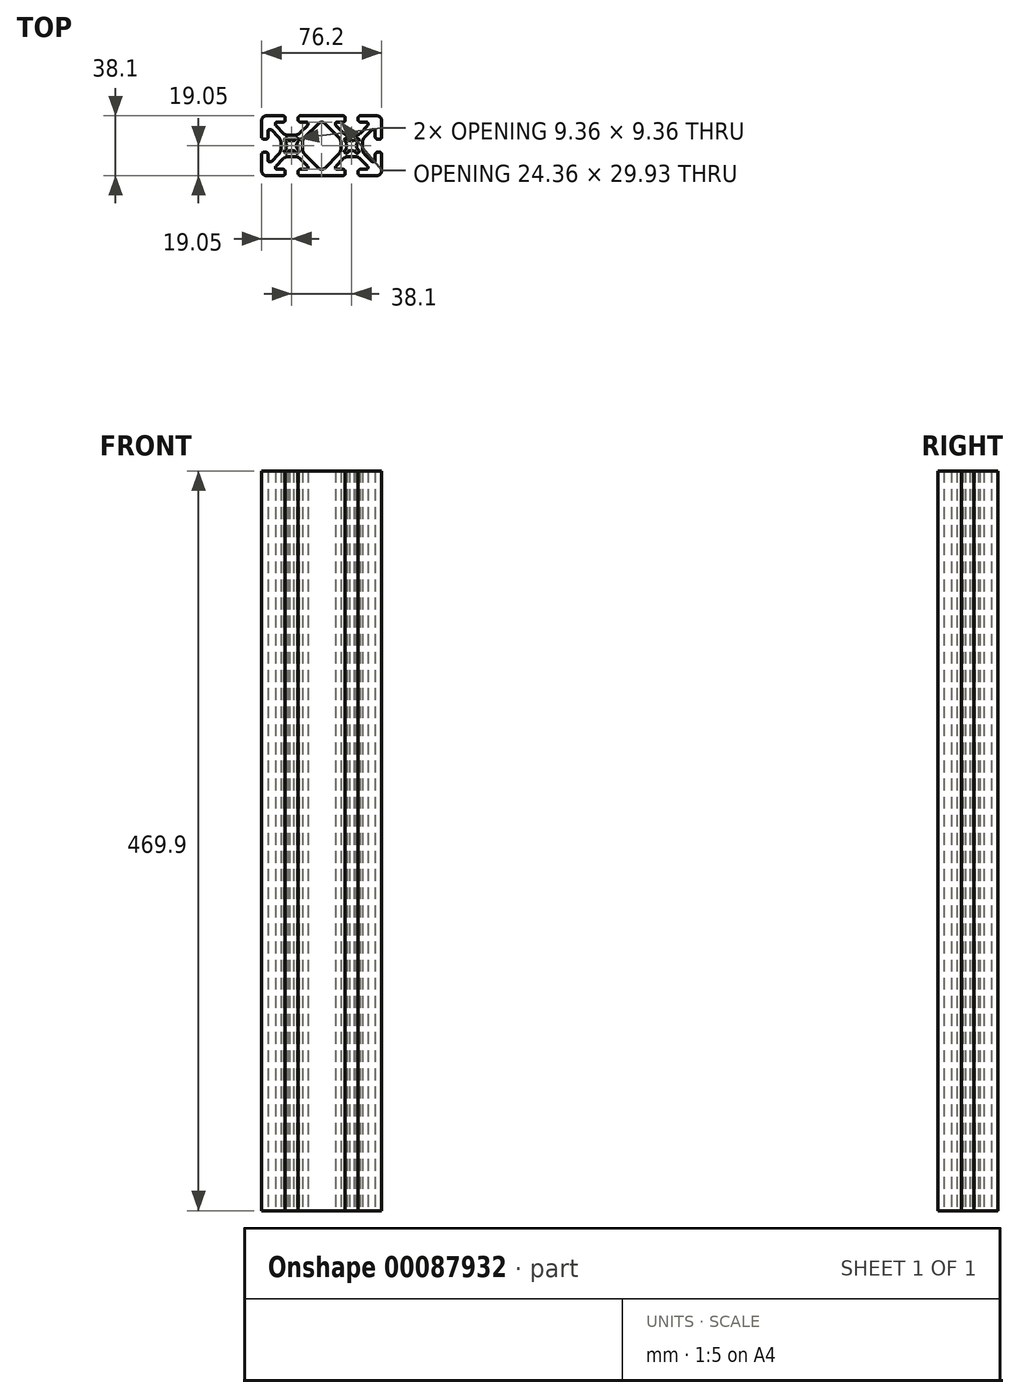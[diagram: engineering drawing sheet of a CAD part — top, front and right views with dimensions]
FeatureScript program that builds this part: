
annotation { "Feature Type Name" : "Feature", "Feature Type Description" : "" }
export const myFeature = defineFeature(function(context is Context, id is Id, definition is map)
    precondition{}
    {
        {
            var Q0;
            Q0=qCreatedBy(makeId("Top.planeOp"),FACE);
            var sketch = newSketch(context, id + "F0", { "sketchPlane" : qUnion([Q0])});
            skLineSegment(sketch, "E0.bottom", {"start": v(-16.18, 38.1) * mm, "end": v(-5.64, 38.1) * mm});
            skLineSegment(sketch, "E0.left", {"start": v(-19.05, 35.23) * mm, "end": v(-19.05, 24.69) * mm});
            skLineSegment(sketch, "E0.right", {"start": v(19.05, 35.23) * mm, "end": v(19.05, 24.69) * mm});
            skPoint(sketch, "E1", {"position": v(0, 19.05) * mm});
            skArc(sketch, "E2", {"start": v(1.35, 22.02) * mm, "mid": v(0, 22.31) * mm, "end": v(-1.35, 22.02) * mm});
            skArc(sketch, "E3", {"start": v(-2.73, 23.4) * mm, "mid": v(-4.35, 23.4) * mm, "end": v(-4.35, 21.78) * mm});
            skArc(sketch, "E4", {"start": v(4.35, 21.78) * mm, "mid": v(4.35, 23.4) * mm, "end": v(2.73, 23.4) * mm});
            skArc(sketch, "E5", {"start": v(2.73, 14.7) * mm, "mid": v(4.35, 14.7) * mm, "end": v(4.35, 16.32) * mm});
            skArc(sketch, "E6", {"start": v(-4.35, 16.32) * mm, "mid": v(-4.35, 14.7) * mm, "end": v(-2.73, 14.7) * mm});
            skLineSegment(sketch, "E7", {"start": v(-2.73, 23.4) * mm, "end": v(-1.35, 22.02) * mm});
            skLineSegment(sketch, "E8", {"start": v(2.73, 23.4) * mm, "end": v(1.35, 22.02) * mm});
            skLineSegment(sketch, "E9", {"start": v(-4.35, 21.78) * mm, "end": v(-2.97, 20.4) * mm});
            skLineSegment(sketch, "E10", {"start": v(-2.73, 14.7) * mm, "end": v(-1.35, 16.08) * mm});
            skLineSegment(sketch, "E11.trimOffspring", {"start": v(2.97, 20.4) * mm, "end": v(4.35, 21.78) * mm});
            skLineSegment(sketch, "E12.trimOffspring", {"start": v(2.97, 17.7) * mm, "end": v(4.35, 16.32) * mm});
            skLineSegment(sketch, "E13.trimOffspring", {"start": v(1.35, 16.08) * mm, "end": v(2.73, 14.7) * mm});
            skLineSegment(sketch, "E14.trimOffspring", {"start": v(-2.97, 17.7) * mm, "end": v(-4.35, 16.32) * mm});
            skArc(sketch, "E15.trimOffspring", {"start": v(2.97, 17.7) * mm, "mid": v(3.26, 19.05) * mm, "end": v(2.97, 20.4) * mm});
            skArc(sketch, "E16.trimOffspring", {"start": v(-1.35, 16.08) * mm, "mid": v(0, 15.79) * mm, "end": v(1.35, 16.08) * mm});
            skArc(sketch, "E17.trimOffspring", {"start": v(-2.97, 20.4) * mm, "mid": v(-3.26, 19.05) * mm, "end": v(-2.97, 17.7) * mm});
            skLineSegment(sketch, "E18.trimOffspring", {"start": v(5.39, 27.31) * mm, "end": v(10.03, 31.95) * mm});
            skLineSegment(sketch, "E19.trimOffspring", {"start": v(7.65, 24.35) * mm, "end": v(12.62, 29.1) * mm});
            skLineSegment(sketch, "E20.trimOffspring", {"start": v(8.14, 13.68) * mm, "end": v(12.84, 9.02) * mm});
            skLineSegment(sketch, "E21.trimOffspring", {"start": v(5.39, 10.79) * mm, "end": v(14.11, 2.07) * mm});
            skArc(sketch, "E22", {"start": v(2.03, 25.92) * mm, "mid": v(3.85, 26.28) * mm, "end": v(5.39, 27.31) * mm});
            skArc(sketch, "E23", {"start": v(6.73, 17.03) * mm, "mid": v(7.1, 15.22) * mm, "end": v(8.14, 13.68) * mm});
            skArc(sketch, "E24", {"start": v(-6.87, 21.08) * mm, "mid": v(-7.23, 22.9) * mm, "end": v(-8.26, 24.44) * mm});
            skArc(sketch, "E25", {"start": v(-2.03, 12.18) * mm, "mid": v(-3.85, 11.82) * mm, "end": v(-5.39, 10.79) * mm});
            skLineSegment(sketch, "E26.trimOffspring", {"start": v(2.03, 25.92) * mm, "end": v(-2.03, 25.92) * mm});
            skLineSegment(sketch, "E27.trimOffspring", {"start": v(6.73, 17.03) * mm, "end": v(6.73, 21.1) * mm});
            skLineSegment(sketch, "E28.trimOffspring", {"start": v(2.03, 12.18) * mm, "end": v(-2.03, 12.18) * mm});
            skLineSegment(sketch, "E29.trimOffspring", {"start": v(-6.87, 17.02) * mm, "end": v(-6.87, 21.08) * mm});
            skPoint(sketch, "E30.right.start.orphan", {"position": v(-6.87, 12.18) * mm});
            skPoint(sketch, "E30.bottom.start.orphan", {"position": v(6.87, 12.18) * mm});
            skPoint(sketch, "E31.trimOffspring.end.orphan", {"position": v(6.87, 25.92) * mm});
            skPoint(sketch, "E32.trimOffspring.end.orphan", {"position": v(-6.87, 25.92) * mm});
            skArc(sketch, "E33.trimOffspring", {"start": v(7.65, 24.35) * mm, "mid": v(6.9, 22.8) * mm, "end": v(6.73, 21.1) * mm});
            skArc(sketch, "E34.trimOffspring", {"start": v(5.39, 10.79) * mm, "mid": v(3.85, 11.82) * mm, "end": v(2.03, 12.18) * mm});
            skArc(sketch, "E35.trimOffspring", {"start": v(-5.39, 27.31) * mm, "mid": v(-3.85, 26.28) * mm, "end": v(-2.03, 25.92) * mm});
            skArc(sketch, "E36.trimOffspring", {"start": v(-8.26, 13.66) * mm, "mid": v(-7.23, 15.2) * mm, "end": v(-6.87, 17.02) * mm});
            skArc(sketch, "E37", {"start": v(14.97, 0) * mm, "mid": v(14.74, 1.12) * mm, "end": v(14.11, 2.07) * mm});
            skArc(sketch, "E38", {"start": v(-14.11, 2.07) * mm, "mid": v(-14.74, 1.12) * mm, "end": v(-14.97, 0) * mm});
            skPoint(sketch, "E39.orphan", {"position": v(-19.05, 38.1) * mm});
            skPoint(sketch, "E40.orphan", {"position": v(19.05, 38.1) * mm});
            skLineSegment(sketch, "E41.trimOffspring", {"start": v(-14.11, 2.07) * mm, "end": v(-5.39, 10.79) * mm});
            skArc(sketch, "E42", {"start": v(-4.06, 36.53) * mm, "mid": v(-4.53, 37.64) * mm, "end": v(-5.64, 38.1) * mm});
            skArc(sketch, "E43", {"start": v(17.48, 23.11) * mm, "mid": v(18.59, 23.58) * mm, "end": v(19.05, 24.69) * mm});
            skArc(sketch, "E44", {"start": v(-16.56, 23.11) * mm, "mid": v(-15.45, 23.58) * mm, "end": v(-14.99, 24.69) * mm});
            skArc(sketch, "E45", {"start": v(-19.05, 24.69) * mm, "mid": v(-18.59, 23.58) * mm, "end": v(-17.48, 23.11) * mm});
            skArc(sketch, "E46", {"start": v(-17.48, 14.99) * mm, "mid": v(-18.59, 14.52) * mm, "end": v(-19.05, 13.41) * mm});
            skArc(sketch, "E47", {"start": v(-14.99, 13.41) * mm, "mid": v(-15.45, 14.52) * mm, "end": v(-16.56, 14.99) * mm});
            skArc(sketch, "E48", {"start": v(16.56, 14.99) * mm, "mid": v(15.45, 14.52) * mm, "end": v(14.99, 13.41) * mm});
            skArc(sketch, "E49", {"start": v(19.05, 13.41) * mm, "mid": v(18.59, 14.52) * mm, "end": v(17.48, 14.99) * mm});
            skArc(sketch, "E50", {"start": v(5.64, 38.1) * mm, "mid": v(4.53, 37.64) * mm, "end": v(4.06, 36.53) * mm});
            skArc(sketch, "E51", {"start": v(4.06, 35.61) * mm, "mid": v(4.53, 34.5) * mm, "end": v(5.64, 34.04) * mm});
            skLineSegment(sketch, "E52", {"start": v(16.56, 23.11) * mm, "end": v(17.48, 23.11) * mm});
            skArc(sketch, "E53", {"start": v(-5.64, 34.04) * mm, "mid": v(-4.53, 34.5) * mm, "end": v(-4.06, 35.61) * mm});
            skArc(sketch, "E54.trimOffspring", {"start": v(14.99, 24.69) * mm, "mid": v(15.45, 23.58) * mm, "end": v(16.56, 23.11) * mm});
            skLineSegment(sketch, "E55", {"start": v(4.06, 36.53) * mm, "end": v(4.06, 35.61) * mm});
            skLineSegment(sketch, "E56", {"start": v(-4.06, 36.53) * mm, "end": v(-4.06, 35.61) * mm});
            skLineSegment(sketch, "E57", {"start": v(-17.48, 23.11) * mm, "end": v(-16.56, 23.11) * mm});
            skLineSegment(sketch, "E58", {"start": v(-17.48, 14.99) * mm, "end": v(-16.56, 14.99) * mm});
            skLineSegment(sketch, "E59", {"start": v(16.56, 14.99) * mm, "end": v(17.48, 14.99) * mm});
            skLineSegment(sketch, "E60.bottom", {"start": v(14.1, 29.34) * mm, "end": v(13.23, 29.34) * mm});
            skLineSegment(sketch, "E60.top", {"start": v(14.1, 8.76) * mm, "end": v(13.47, 8.76) * mm});
            skLineSegment(sketch, "E60.left", {"start": v(14.99, 28.45) * mm, "end": v(14.99, 24.69) * mm});
            skLineSegment(sketch, "E60.right", {"start": v(-14.99, 28.45) * mm, "end": v(-14.99, 24.69) * mm});
            skLineSegment(sketch, "E61.bottom", {"start": v(-9.4, 34.04) * mm, "end": v(-5.64, 34.04) * mm});
            skLineSegment(sketch, "E61.left", {"start": v(-10.29, 33.15) * mm, "end": v(-10.29, 32.58) * mm});
            skLineSegment(sketch, "E61.right", {"start": v(10.29, 33.15) * mm, "end": v(10.29, 32.58) * mm});
            skArc(sketch, "E62", {"start": v(-9.4, 34.04) * mm, "mid": v(-10.03, 33.78) * mm, "end": v(-10.29, 33.15) * mm});
            skArc(sketch, "E63", {"start": v(10.29, 33.15) * mm, "mid": v(10.03, 33.78) * mm, "end": v(9.4, 34.04) * mm});
            skArc(sketch, "E64", {"start": v(10.03, 31.95) * mm, "mid": v(10.22, 32.24) * mm, "end": v(10.29, 32.58) * mm});
            skArc(sketch, "E65", {"start": v(-14.1, 29.34) * mm, "mid": v(-14.73, 29.08) * mm, "end": v(-14.99, 28.45) * mm});
            skArc(sketch, "E66", {"start": v(-13.53, 8.76) * mm, "mid": v(-13.19, 8.83) * mm, "end": v(-12.9, 9.02) * mm});
            skArc(sketch, "E67", {"start": v(14.1, 8.76) * mm, "mid": v(14.73, 9.02) * mm, "end": v(14.99, 9.65) * mm});
            skLineSegment(sketch, "E68.trimOffspring", {"start": v(-13.53, 8.76) * mm, "end": v(-14.1, 8.76) * mm});
            skLineSegment(sketch, "E69.trimOffspring", {"start": v(-12.9, 9.02) * mm, "end": v(-8.26, 13.66) * mm});
            skArc(sketch, "E70.trimOffspring", {"start": v(-14.99, 9.65) * mm, "mid": v(-14.73, 9.02) * mm, "end": v(-14.1, 8.76) * mm});
            skLineSegment(sketch, "E71.trimOffspring", {"start": v(-13.53, 29.34) * mm, "end": v(-14.1, 29.34) * mm});
            skLineSegment(sketch, "E72.trimOffspring", {"start": v(-12.9, 29.08) * mm, "end": v(-8.26, 24.44) * mm});
            skArc(sketch, "E73.trimOffspring", {"start": v(-12.9, 29.08) * mm, "mid": v(-13.19, 29.27) * mm, "end": v(-13.53, 29.34) * mm});
            skArc(sketch, "E74.trimOffspring", {"start": v(-10.29, 32.58) * mm, "mid": v(-10.22, 32.24) * mm, "end": v(-10.03, 31.95) * mm});
            skLineSegment(sketch, "E75.trimOffspring", {"start": v(-10.03, 31.95) * mm, "end": v(-5.39, 27.31) * mm});
            skLineSegment(sketch, "E76.trimOffspring", {"start": v(5.64, 34.04) * mm, "end": v(9.4, 34.04) * mm});
            skLineSegment(sketch, "E77.trimOffspring", {"start": v(5.64, 38.1) * mm, "end": v(16.18, 38.1) * mm});
            skArc(sketch, "E78.trimOffspring", {"start": v(13.23, 29.34) * mm, "mid": v(12.9, 29.27) * mm, "end": v(12.62, 29.1) * mm});
            skArc(sketch, "E79.trimOffspring", {"start": v(14.99, 28.45) * mm, "mid": v(14.73, 29.08) * mm, "end": v(14.1, 29.34) * mm});
            skArc(sketch, "E80.trimOffspring", {"start": v(12.84, 9.02) * mm, "mid": v(13.13, 8.83) * mm, "end": v(13.47, 8.76) * mm});
            skLineSegment(sketch, "E81.trimOffspring", {"start": v(14.99, 13.41) * mm, "end": v(14.99, 9.65) * mm});
            skLineSegment(sketch, "E82.trimOffspring", {"start": v(-14.99, 13.41) * mm, "end": v(-14.99, 9.65) * mm});
            skArc(sketch, "E83.trimOffspring", {"start": v(-15.88, 38.1) * mm, "mid": v(-18.12, 37.17) * mm, "end": v(-19.05, 34.92) * mm});
            skArc(sketch, "E84.trimOffspring", {"start": v(19.05, 34.92) * mm, "mid": v(18.12, 37.17) * mm, "end": v(15.87, 38.1) * mm});
            skLineSegment(sketch, "E85.trimOffspring", {"start": v(-19.05, 13.41) * mm, "end": v(-19.05, 0) * mm});
            skLineSegment(sketch, "E86.trimOffspring", {"start": v(19.05, 13.41) * mm, "end": v(19.05, 0) * mm});
            skLineSegment(sketch, "E87", {"start": v(-19.05, 0) * mm, "end": v(19.05, 0) * mm, "construction": true});
            skLineSegment(sketch, "E88.MirrorCS", {"start": v(10.29, -33.15) * mm, "end": v(10.29, -32.58) * mm});
            skArc(sketch, "E89.MirrorCS", {"start": v(10.03, -31.95) * mm, "mid": v(10.22, -32.24) * mm, "end": v(10.29, -32.58) * mm});
            skArc(sketch, "E90.MirrorCS", {"start": v(-9.4, -34.04) * mm, "mid": v(-10.03, -33.78) * mm, "end": v(-10.29, -33.15) * mm});
            skArc(sketch, "E91.MirrorCS", {"start": v(10.29, -33.15) * mm, "mid": v(10.03, -33.78) * mm, "end": v(9.4, -34.04) * mm});
            skArc(sketch, "E92.MirrorCS", {"start": v(14.99, -28.45) * mm, "mid": v(14.73, -29.08) * mm, "end": v(14.1, -29.34) * mm});
            skArc(sketch, "E93.MirrorCS", {"start": v(-14.99, -9.65) * mm, "mid": v(-14.73, -9.02) * mm, "end": v(-14.1, -8.76) * mm});
            skPoint(sketch, "E94.MirrorP", {"position": v(0, -19.05) * mm});
            skArc(sketch, "E95.MirrorCS", {"start": v(-14.1, -29.34) * mm, "mid": v(-14.73, -29.08) * mm, "end": v(-14.99, -28.45) * mm});
            skLineSegment(sketch, "E96.MirrorCS", {"start": v(4.06, -36.53) * mm, "end": v(4.06, -35.61) * mm});
            skLineSegment(sketch, "E97.MirrorCS", {"start": v(16.56, -14.99) * mm, "end": v(17.48, -14.99) * mm});
            skLineSegment(sketch, "E98.MirrorCS", {"start": v(-4.35, -21.78) * mm, "end": v(-2.97, -20.4) * mm});
            skLineSegment(sketch, "E99.MirrorCS", {"start": v(2.97, -20.4) * mm, "end": v(4.35, -21.78) * mm});
            skLineSegment(sketch, "E100.MirrorCS", {"start": v(-17.48, -23.11) * mm, "end": v(-16.56, -23.11) * mm});
            skArc(sketch, "E101.MirrorCS", {"start": v(16.56, -14.99) * mm, "mid": v(15.45, -14.52) * mm, "end": v(14.99, -13.41) * mm});
            skLineSegment(sketch, "E102.MirrorCS", {"start": v(-2.97, -17.7) * mm, "end": v(-4.35, -16.32) * mm});
            skLineSegment(sketch, "E103.MirrorCS", {"start": v(1.35, -16.08) * mm, "end": v(2.73, -14.7) * mm});
            skLineSegment(sketch, "E104.MirrorCS", {"start": v(2.97, -17.7) * mm, "end": v(4.35, -16.32) * mm});
            skLineSegment(sketch, "E105.MirrorCS", {"start": v(-13.53, -8.76) * mm, "end": v(-14.1, -8.76) * mm});
            skArc(sketch, "E106.MirrorCS", {"start": v(14.1, -8.76) * mm, "mid": v(14.73, -9.02) * mm, "end": v(14.99, -9.65) * mm});
            skArc(sketch, "E107.MirrorCS", {"start": v(-10.29, -32.58) * mm, "mid": v(-10.22, -32.24) * mm, "end": v(-10.03, -31.95) * mm});
            skLineSegment(sketch, "E108.MirrorCS", {"start": v(-17.48, -14.99) * mm, "end": v(-16.56, -14.99) * mm});
            skArc(sketch, "E109.MirrorCS", {"start": v(-14.99, -13.41) * mm, "mid": v(-15.45, -14.52) * mm, "end": v(-16.56, -14.99) * mm});
            skLineSegment(sketch, "E110.MirrorCS", {"start": v(-10.29, -33.15) * mm, "end": v(-10.29, -32.58) * mm});
            skLineSegment(sketch, "E111.MirrorCS", {"start": v(14.1, -29.34) * mm, "end": v(13.23, -29.34) * mm});
            skArc(sketch, "E112.MirrorCS", {"start": v(-16.56, -23.11) * mm, "mid": v(-15.45, -23.58) * mm, "end": v(-14.99, -24.69) * mm});
            skArc(sketch, "E113.MirrorCS", {"start": v(-13.53, -8.76) * mm, "mid": v(-13.19, -8.83) * mm, "end": v(-12.9, -9.02) * mm});
            skArc(sketch, "E114.MirrorCS", {"start": v(13.23, -29.34) * mm, "mid": v(12.9, -29.27) * mm, "end": v(12.62, -29.1) * mm});
            skLineSegment(sketch, "E115.MirrorCS", {"start": v(-2.73, -23.4) * mm, "end": v(-1.35, -22.02) * mm});
            skArc(sketch, "E116.MirrorCS", {"start": v(-12.9, -29.08) * mm, "mid": v(-13.19, -29.27) * mm, "end": v(-13.53, -29.34) * mm});
            skLineSegment(sketch, "E117.MirrorCS", {"start": v(2.73, -23.4) * mm, "end": v(1.35, -22.02) * mm});
            skArc(sketch, "E118.MirrorCS", {"start": v(-17.48, -14.99) * mm, "mid": v(-18.59, -14.52) * mm, "end": v(-19.05, -13.41) * mm});
            skLineSegment(sketch, "E119.MirrorCS", {"start": v(16.56, -23.11) * mm, "end": v(17.48, -23.11) * mm});
            skArc(sketch, "E120.MirrorCS", {"start": v(-19.05, -24.69) * mm, "mid": v(-18.59, -23.58) * mm, "end": v(-17.48, -23.11) * mm});
            skArc(sketch, "E121.MirrorCS", {"start": v(12.84, -9.02) * mm, "mid": v(13.13, -8.83) * mm, "end": v(13.47, -8.76) * mm});
            skLineSegment(sketch, "E122.MirrorCS", {"start": v(-13.53, -29.34) * mm, "end": v(-14.1, -29.34) * mm});
            skLineSegment(sketch, "E123.MirrorCS", {"start": v(14.1, -8.76) * mm, "end": v(13.47, -8.76) * mm});
            skLineSegment(sketch, "E124.MirrorCS", {"start": v(-4.06, -36.53) * mm, "end": v(-4.06, -35.61) * mm});
            skLineSegment(sketch, "E125.MirrorCS", {"start": v(-2.73, -14.7) * mm, "end": v(-1.35, -16.08) * mm});
            skArc(sketch, "E126.MirrorCS", {"start": v(4.35, -21.78) * mm, "mid": v(4.35, -23.4) * mm, "end": v(2.73, -23.4) * mm});
            skArc(sketch, "E127.MirrorCS", {"start": v(1.35, -22.02) * mm, "mid": v(0, -22.31) * mm, "end": v(-1.35, -22.02) * mm});
            skArc(sketch, "E128.MirrorCS", {"start": v(14.99, -24.69) * mm, "mid": v(15.45, -23.58) * mm, "end": v(16.56, -23.11) * mm});
            skLineSegment(sketch, "E129.MirrorCS", {"start": v(14.99, -13.41) * mm, "end": v(14.99, -9.65) * mm});
            skArc(sketch, "E130.MirrorCS", {"start": v(-14.11, -2.07) * mm, "mid": v(-14.74, -1.12) * mm, "end": v(-14.97, 0) * mm});
            skLineSegment(sketch, "E131.MirrorCS", {"start": v(5.64, -34.04) * mm, "end": v(9.4, -34.04) * mm});
            skArc(sketch, "E132.MirrorCS", {"start": v(19.05, -13.41) * mm, "mid": v(18.59, -14.52) * mm, "end": v(17.48, -14.99) * mm});
            skLineSegment(sketch, "E133.MirrorCS", {"start": v(-6.87, -17.02) * mm, "end": v(-6.87, -21.08) * mm});
            skLineSegment(sketch, "E134.MirrorCS", {"start": v(-14.99, -13.41) * mm, "end": v(-14.99, -9.65) * mm});
            skLineSegment(sketch, "E135.MirrorCS", {"start": v(14.99, -28.45) * mm, "end": v(14.99, -24.69) * mm});
            skLineSegment(sketch, "E136.MirrorCS", {"start": v(-9.4, -34.04) * mm, "end": v(-5.64, -34.04) * mm});
            skArc(sketch, "E137.MirrorCS", {"start": v(17.48, -23.11) * mm, "mid": v(18.59, -23.58) * mm, "end": v(19.05, -24.69) * mm});
            skArc(sketch, "E138.MirrorCS", {"start": v(14.97, 0) * mm, "mid": v(14.74, -1.12) * mm, "end": v(14.11, -2.07) * mm});
            skLineSegment(sketch, "E139.MirrorCS", {"start": v(-14.99, -28.45) * mm, "end": v(-14.99, -24.69) * mm});
            skArc(sketch, "E140.MirrorCS", {"start": v(-2.97, -20.4) * mm, "mid": v(-3.26, -19.05) * mm, "end": v(-2.97, -17.7) * mm});
            skLineSegment(sketch, "E141.MirrorCS", {"start": v(5.39, -27.31) * mm, "end": v(10.03, -31.95) * mm});
            skArc(sketch, "E142.MirrorCS", {"start": v(-1.35, -16.08) * mm, "mid": v(0, -15.79) * mm, "end": v(1.35, -16.08) * mm});
            skArc(sketch, "E143.MirrorCS", {"start": v(-8.26, -13.66) * mm, "mid": v(-7.23, -15.2) * mm, "end": v(-6.87, -17.02) * mm});
            skArc(sketch, "E144.MirrorCS", {"start": v(2.73, -14.7) * mm, "mid": v(4.35, -14.7) * mm, "end": v(4.35, -16.32) * mm});
            skLineSegment(sketch, "E145.MirrorCS", {"start": v(-14.11, -2.07) * mm, "end": v(-5.39, -10.79) * mm});
            skArc(sketch, "E146.MirrorCS", {"start": v(-2.73, -23.4) * mm, "mid": v(-4.35, -23.4) * mm, "end": v(-4.35, -21.78) * mm});
            skLineSegment(sketch, "E147.MirrorCS", {"start": v(19.05, -35.23) * mm, "end": v(19.05, -24.69) * mm});
            skLineSegment(sketch, "E148.MirrorCS", {"start": v(-19.05, -35.23) * mm, "end": v(-19.05, -24.69) * mm});
            skLineSegment(sketch, "E149.MirrorCS", {"start": v(-16.18, -38.1) * mm, "end": v(-5.64, -38.1) * mm});
            skPoint(sketch, "E150.MirrorP", {"position": v(6.87, -12.18) * mm});
            skArc(sketch, "E151.MirrorCS", {"start": v(7.65, -24.35) * mm, "mid": v(6.9, -22.8) * mm, "end": v(6.73, -21.1) * mm});
            skArc(sketch, "E152.MirrorCS", {"start": v(-4.06, -36.53) * mm, "mid": v(-4.53, -37.64) * mm, "end": v(-5.64, -38.1) * mm});
            skArc(sketch, "E153.MirrorCS", {"start": v(4.06, -35.61) * mm, "mid": v(4.53, -34.5) * mm, "end": v(5.64, -34.04) * mm});
            skArc(sketch, "E154.MirrorCS", {"start": v(-6.87, -21.08) * mm, "mid": v(-7.23, -22.9) * mm, "end": v(-8.26, -24.44) * mm});
            skLineSegment(sketch, "E155.MirrorCS", {"start": v(5.39, -10.79) * mm, "end": v(14.11, -2.07) * mm});
            skArc(sketch, "E156.MirrorCS", {"start": v(-4.35, -16.32) * mm, "mid": v(-4.35, -14.7) * mm, "end": v(-2.73, -14.7) * mm});
            skPoint(sketch, "E157.MirrorP", {"position": v(-6.87, -12.18) * mm});
            skPoint(sketch, "E158.MirrorP", {"position": v(-6.87, -25.92) * mm});
            skArc(sketch, "E159.MirrorCS", {"start": v(6.73, -17.03) * mm, "mid": v(7.1, -15.22) * mm, "end": v(8.14, -13.68) * mm});
            skLineSegment(sketch, "E160.MirrorCS", {"start": v(-12.9, -9.02) * mm, "end": v(-8.26, -13.66) * mm});
            skPoint(sketch, "E161.MirrorP", {"position": v(6.87, -25.92) * mm});
            skArc(sketch, "E162.MirrorCS", {"start": v(19.05, -34.92) * mm, "mid": v(18.12, -37.17) * mm, "end": v(15.87, -38.1) * mm});
            skPoint(sketch, "E163.MirrorP", {"position": v(-19.05, -38.1) * mm});
            skArc(sketch, "E164.MirrorCS", {"start": v(5.39, -10.79) * mm, "mid": v(3.85, -11.82) * mm, "end": v(2.03, -12.18) * mm});
            skArc(sketch, "E165.MirrorCS", {"start": v(-2.03, -12.18) * mm, "mid": v(-3.85, -11.82) * mm, "end": v(-5.39, -10.79) * mm});
            skLineSegment(sketch, "E166.MirrorCS", {"start": v(-12.9, -29.08) * mm, "end": v(-8.26, -24.44) * mm});
            skArc(sketch, "E167.MirrorCS", {"start": v(2.97, -17.7) * mm, "mid": v(3.26, -19.05) * mm, "end": v(2.97, -20.4) * mm});
            skLineSegment(sketch, "E168.MirrorCS", {"start": v(19.05, -13.41) * mm, "end": v(19.05, 0) * mm});
            skLineSegment(sketch, "E169.MirrorCS", {"start": v(-10.03, -31.95) * mm, "end": v(-5.39, -27.31) * mm});
            skLineSegment(sketch, "E170.MirrorCS", {"start": v(8.14, -13.68) * mm, "end": v(12.84, -9.02) * mm});
            skLineSegment(sketch, "E171.MirrorCS", {"start": v(-19.05, -13.41) * mm, "end": v(-19.05, 0) * mm});
            skLineSegment(sketch, "E172.MirrorCS", {"start": v(6.73, -17.03) * mm, "end": v(6.73, -21.1) * mm});
            skArc(sketch, "E173.MirrorCS", {"start": v(-15.87, -38.1) * mm, "mid": v(-18.12, -37.17) * mm, "end": v(-19.05, -34.92) * mm});
            skArc(sketch, "E174.MirrorCS", {"start": v(5.64, -38.1) * mm, "mid": v(4.53, -37.64) * mm, "end": v(4.06, -36.53) * mm});
            skLineSegment(sketch, "E175.MirrorCS", {"start": v(5.64, -38.1) * mm, "end": v(16.18, -38.1) * mm});
            skLineSegment(sketch, "E176.MirrorCS", {"start": v(2.03, -12.18) * mm, "end": v(-2.03, -12.18) * mm});
            skArc(sketch, "E177.MirrorCS", {"start": v(-5.39, -27.31) * mm, "mid": v(-3.85, -26.28) * mm, "end": v(-2.03, -25.92) * mm});
            skPoint(sketch, "E178.MirrorP", {"position": v(19.05, -38.1) * mm});
            skArc(sketch, "E179.MirrorCS", {"start": v(-5.64, -34.04) * mm, "mid": v(-4.53, -34.5) * mm, "end": v(-4.06, -35.61) * mm});
            skArc(sketch, "E180.MirrorCS", {"start": v(2.03, -25.92) * mm, "mid": v(3.85, -26.28) * mm, "end": v(5.39, -27.31) * mm});
            skLineSegment(sketch, "E181.MirrorCS", {"start": v(2.03, -25.92) * mm, "end": v(-2.03, -25.92) * mm});
            skLineSegment(sketch, "E182.MirrorCS", {"start": v(7.65, -24.35) * mm, "end": v(12.62, -29.1) * mm});
            skSolve(sketch);
        }
        {
            var Q0;
            Q0=qCreatedBy(makeId("Right.planeOp"),FACE);
            var sketch = newSketch(context, id + "F1", { "sketchPlane" : qUnion([Q0])});
            skLineSegment(sketch, "E183", {"start": v(0, 0) * mm, "end": v(0, 73.05) * mm, "construction": true});
            skLineSegment(sketch, "E184", {"start": v(0, 0) * mm, "end": v(0, -75.8) * mm, "construction": true});
            skLineSegment(sketch, "E185", {"start": v(0, 73.05) * mm, "end": v(0, 320.06) * mm, "construction": true});
            skLineSegment(sketch, "E186", {"start": v(0, -75.8) * mm, "end": v(2.77, -215.96) * mm, "construction": true});
            skSolve(sketch);
        }
        {
            var Q0;
            Q0 = qSketchRegion(id + "F0", true);
            extrude(context, id + "F2", {"entities" : qUnion([Q0]), "endBound" : BoundingType.SYMMETRIC, "depth" : 469.9 * mm});
        }
        {
            var Q0;
            Q0=makeQuery(id+"F2.opExtrude","SWEPT_BODY",BODY,{"disambiguationData":[OSD([sQuery(id+"F0.wireOp",EDGE,"E0.bottom"),sQuery(id+"F0.wireOp",EDGE,"E0.left"),sQuery(id+"F0.wireOp",EDGE,"E0.right"),sQuery(id+"F0.wireOp",EDGE,"E2"),sQuery(id+"F0.wireOp",EDGE,"E3"),sQuery(id+"F0.wireOp",EDGE,"E4"),sQuery(id+"F0.wireOp",EDGE,"E5"),sQuery(id+"F0.wireOp",EDGE,"E6"),sQuery(id+"F0.wireOp",EDGE,"E7"),sQuery(id+"F0.wireOp",EDGE,"E8"),sQuery(id+"F0.wireOp",EDGE,"E9"),sQuery(id+"F0.wireOp",EDGE,"E10"),sQuery(id+"F0.wireOp",EDGE,"E11.trimOffspring"),sQuery(id+"F0.wireOp",EDGE,"E12.trimOffspring"),sQuery(id+"F0.wireOp",EDGE,"E13.trimOffspring"),sQuery(id+"F0.wireOp",EDGE,"E14.trimOffspring"),sQuery(id+"F0.wireOp",EDGE,"E15.trimOffspring"),sQuery(id+"F0.wireOp",EDGE,"E16.trimOffspring"),sQuery(id+"F0.wireOp",EDGE,"E17.trimOffspring"),sQuery(id+"F0.wireOp",EDGE,"E18.trimOffspring"),sQuery(id+"F0.wireOp",EDGE,"E19.trimOffspring"),sQuery(id+"F0.wireOp",EDGE,"E20.trimOffspring"),sQuery(id+"F0.wireOp",EDGE,"E21.trimOffspring"),sQuery(id+"F0.wireOp",EDGE,"E22"),sQuery(id+"F0.wireOp",EDGE,"E23"),sQuery(id+"F0.wireOp",EDGE,"E24"),sQuery(id+"F0.wireOp",EDGE,"E25"),sQuery(id+"F0.wireOp",EDGE,"E26.trimOffspring"),sQuery(id+"F0.wireOp",EDGE,"E27.trimOffspring"),sQuery(id+"F0.wireOp",EDGE,"E28.trimOffspring"),sQuery(id+"F0.wireOp",EDGE,"E29.trimOffspring"),sQuery(id+"F0.wireOp",EDGE,"E33.trimOffspring"),sQuery(id+"F0.wireOp",EDGE,"E34.trimOffspring"),sQuery(id+"F0.wireOp",EDGE,"E35.trimOffspring"),sQuery(id+"F0.wireOp",EDGE,"E36.trimOffspring"),sQuery(id+"F0.wireOp",EDGE,"E37"),sQuery(id+"F0.wireOp",EDGE,"E38"),sQuery(id+"F0.wireOp",EDGE,"E41.trimOffspring"),sQuery(id+"F0.wireOp",EDGE,"E42"),sQuery(id+"F0.wireOp",EDGE,"E43"),sQuery(id+"F0.wireOp",EDGE,"E44"),sQuery(id+"F0.wireOp",EDGE,"E45"),sQuery(id+"F0.wireOp",EDGE,"E46"),sQuery(id+"F0.wireOp",EDGE,"E47"),sQuery(id+"F0.wireOp",EDGE,"E48"),sQuery(id+"F0.wireOp",EDGE,"E49"),sQuery(id+"F0.wireOp",EDGE,"E50"),sQuery(id+"F0.wireOp",EDGE,"E51"),sQuery(id+"F0.wireOp",EDGE,"E52"),sQuery(id+"F0.wireOp",EDGE,"E53"),sQuery(id+"F0.wireOp",EDGE,"E54.trimOffspring"),sQuery(id+"F0.wireOp",EDGE,"E55"),sQuery(id+"F0.wireOp",EDGE,"E56"),sQuery(id+"F0.wireOp",EDGE,"E57"),sQuery(id+"F0.wireOp",EDGE,"E58"),sQuery(id+"F0.wireOp",EDGE,"E59"),sQuery(id+"F0.wireOp",EDGE,"E60.bottom"),sQuery(id+"F0.wireOp",EDGE,"E60.top"),sQuery(id+"F0.wireOp",EDGE,"E61.left"),sQuery(id+"F0.wireOp",EDGE,"E61.right"),sQuery(id+"F0.wireOp",EDGE,"E62"),sQuery(id+"F0.wireOp",EDGE,"E63"),sQuery(id+"F0.wireOp",EDGE,"E64"),sQuery(id+"F0.wireOp",EDGE,"E65"),sQuery(id+"F0.wireOp",EDGE,"E66"),sQuery(id+"F0.wireOp",EDGE,"E67"),sQuery(id+"F0.wireOp",EDGE,"E68.trimOffspring"),sQuery(id+"F0.wireOp",EDGE,"E69.trimOffspring"),sQuery(id+"F0.wireOp",EDGE,"E70.trimOffspring"),sQuery(id+"F0.wireOp",EDGE,"E60.right"),sQuery(id+"F0.wireOp",EDGE,"E71.trimOffspring"),sQuery(id+"F0.wireOp",EDGE,"E72.trimOffspring"),sQuery(id+"F0.wireOp",EDGE,"E73.trimOffspring"),sQuery(id+"F0.wireOp",EDGE,"E61.bottom"),sQuery(id+"F0.wireOp",EDGE,"E74.trimOffspring"),sQuery(id+"F0.wireOp",EDGE,"E75.trimOffspring"),sQuery(id+"F0.wireOp",EDGE,"E76.trimOffspring"),sQuery(id+"F0.wireOp",EDGE,"E77.trimOffspring"),sQuery(id+"F0.wireOp",EDGE,"E78.trimOffspring"),sQuery(id+"F0.wireOp",EDGE,"E79.trimOffspring"),sQuery(id+"F0.wireOp",EDGE,"E60.left"),sQuery(id+"F0.wireOp",EDGE,"E80.trimOffspring"),sQuery(id+"F0.wireOp",EDGE,"E81.trimOffspring"),sQuery(id+"F0.wireOp",EDGE,"E83.trimOffspring"),sQuery(id+"F0.wireOp",EDGE,"E84.trimOffspring"),sQuery(id+"F0.wireOp",EDGE,"E82.trimOffspring"),sQuery(id+"F0.wireOp",EDGE,"E85.trimOffspring"),sQuery(id+"F0.wireOp",EDGE,"E86.trimOffspring"),sQuery(id+"F0.wireOp",EDGE,"E88.MirrorCS"),sQuery(id+"F0.wireOp",EDGE,"E89.MirrorCS"),sQuery(id+"F0.wireOp",EDGE,"E90.MirrorCS"),sQuery(id+"F0.wireOp",EDGE,"E91.MirrorCS"),sQuery(id+"F0.wireOp",EDGE,"E92.MirrorCS"),sQuery(id+"F0.wireOp",EDGE,"E93.MirrorCS"),sQuery(id+"F0.wireOp",EDGE,"E95.MirrorCS"),sQuery(id+"F0.wireOp",EDGE,"E96.MirrorCS"),sQuery(id+"F0.wireOp",EDGE,"E97.MirrorCS"),sQuery(id+"F0.wireOp",EDGE,"E98.MirrorCS"),sQuery(id+"F0.wireOp",EDGE,"E99.MirrorCS"),sQuery(id+"F0.wireOp",EDGE,"E100.MirrorCS"),sQuery(id+"F0.wireOp",EDGE,"E101.MirrorCS"),sQuery(id+"F0.wireOp",EDGE,"E102.MirrorCS"),sQuery(id+"F0.wireOp",EDGE,"E103.MirrorCS"),sQuery(id+"F0.wireOp",EDGE,"E104.MirrorCS"),sQuery(id+"F0.wireOp",EDGE,"E105.MirrorCS"),sQuery(id+"F0.wireOp",EDGE,"E106.MirrorCS"),sQuery(id+"F0.wireOp",EDGE,"E107.MirrorCS"),sQuery(id+"F0.wireOp",EDGE,"E108.MirrorCS"),sQuery(id+"F0.wireOp",EDGE,"E109.MirrorCS"),sQuery(id+"F0.wireOp",EDGE,"E110.MirrorCS"),sQuery(id+"F0.wireOp",EDGE,"E111.MirrorCS"),sQuery(id+"F0.wireOp",EDGE,"E112.MirrorCS"),sQuery(id+"F0.wireOp",EDGE,"E113.MirrorCS"),sQuery(id+"F0.wireOp",EDGE,"E114.MirrorCS"),sQuery(id+"F0.wireOp",EDGE,"E115.MirrorCS"),sQuery(id+"F0.wireOp",EDGE,"E116.MirrorCS"),sQuery(id+"F0.wireOp",EDGE,"E117.MirrorCS"),sQuery(id+"F0.wireOp",EDGE,"E118.MirrorCS"),sQuery(id+"F0.wireOp",EDGE,"E119.MirrorCS"),sQuery(id+"F0.wireOp",EDGE,"E120.MirrorCS"),sQuery(id+"F0.wireOp",EDGE,"E121.MirrorCS"),sQuery(id+"F0.wireOp",EDGE,"E122.MirrorCS"),sQuery(id+"F0.wireOp",EDGE,"E123.MirrorCS"),sQuery(id+"F0.wireOp",EDGE,"E124.MirrorCS"),sQuery(id+"F0.wireOp",EDGE,"E125.MirrorCS"),sQuery(id+"F0.wireOp",EDGE,"E126.MirrorCS"),sQuery(id+"F0.wireOp",EDGE,"E127.MirrorCS"),sQuery(id+"F0.wireOp",EDGE,"E128.MirrorCS"),sQuery(id+"F0.wireOp",EDGE,"E130.MirrorCS"),sQuery(id+"F0.wireOp",EDGE,"E132.MirrorCS"),sQuery(id+"F0.wireOp",EDGE,"E133.MirrorCS"),sQuery(id+"F0.wireOp",EDGE,"E137.MirrorCS"),sQuery(id+"F0.wireOp",EDGE,"E138.MirrorCS"),sQuery(id+"F0.wireOp",EDGE,"E140.MirrorCS"),sQuery(id+"F0.wireOp",EDGE,"E141.MirrorCS"),sQuery(id+"F0.wireOp",EDGE,"E142.MirrorCS"),sQuery(id+"F0.wireOp",EDGE,"E143.MirrorCS"),sQuery(id+"F0.wireOp",EDGE,"E144.MirrorCS"),sQuery(id+"F0.wireOp",EDGE,"E145.MirrorCS"),sQuery(id+"F0.wireOp",EDGE,"E146.MirrorCS"),sQuery(id+"F0.wireOp",EDGE,"E147.MirrorCS"),sQuery(id+"F0.wireOp",EDGE,"E148.MirrorCS"),sQuery(id+"F0.wireOp",EDGE,"E149.MirrorCS"),sQuery(id+"F0.wireOp",EDGE,"E151.MirrorCS"),sQuery(id+"F0.wireOp",EDGE,"E152.MirrorCS"),sQuery(id+"F0.wireOp",EDGE,"E153.MirrorCS"),sQuery(id+"F0.wireOp",EDGE,"E154.MirrorCS"),sQuery(id+"F0.wireOp",EDGE,"E155.MirrorCS"),sQuery(id+"F0.wireOp",EDGE,"E156.MirrorCS"),sQuery(id+"F0.wireOp",EDGE,"E159.MirrorCS"),sQuery(id+"F0.wireOp",EDGE,"E160.MirrorCS"),sQuery(id+"F0.wireOp",EDGE,"E134.MirrorCS"),sQuery(id+"F0.wireOp",EDGE,"E162.MirrorCS"),sQuery(id+"F0.wireOp",EDGE,"E164.MirrorCS"),sQuery(id+"F0.wireOp",EDGE,"E165.MirrorCS"),sQuery(id+"F0.wireOp",EDGE,"E166.MirrorCS"),sQuery(id+"F0.wireOp",EDGE,"E167.MirrorCS"),sQuery(id+"F0.wireOp",EDGE,"E168.MirrorCS"),sQuery(id+"F0.wireOp",EDGE,"E169.MirrorCS"),sQuery(id+"F0.wireOp",EDGE,"E136.MirrorCS"),sQuery(id+"F0.wireOp",EDGE,"E170.MirrorCS"),sQuery(id+"F0.wireOp",EDGE,"E171.MirrorCS"),sQuery(id+"F0.wireOp",EDGE,"E172.MirrorCS"),sQuery(id+"F0.wireOp",EDGE,"E173.MirrorCS"),sQuery(id+"F0.wireOp",EDGE,"E174.MirrorCS"),sQuery(id+"F0.wireOp",EDGE,"E131.MirrorCS"),sQuery(id+"F0.wireOp",EDGE,"E175.MirrorCS"),sQuery(id+"F0.wireOp",EDGE,"E176.MirrorCS"),sQuery(id+"F0.wireOp",EDGE,"E129.MirrorCS"),sQuery(id+"F0.wireOp",EDGE,"E177.MirrorCS"),sQuery(id+"F0.wireOp",EDGE,"E179.MirrorCS"),sQuery(id+"F0.wireOp",EDGE,"E180.MirrorCS"),sQuery(id+"F0.wireOp",EDGE,"E139.MirrorCS"),sQuery(id+"F0.wireOp",EDGE,"E135.MirrorCS"),sQuery(id+"F0.wireOp",EDGE,"E181.MirrorCS"),sQuery(id+"F0.wireOp",EDGE,"E182.MirrorCS")])]});
            var Q1;
            Q1=sQuery(id+"F1.wireOp",EDGE,"E185");
            transform(context, id + "F3", {"entities" : qUnion([Q0]), "transformType" : TransformType.ROTATION, "transformAxis" : qUnion([Q1]), "angle" : 90 * degree, "makeCopy" : false});
        }
    });
